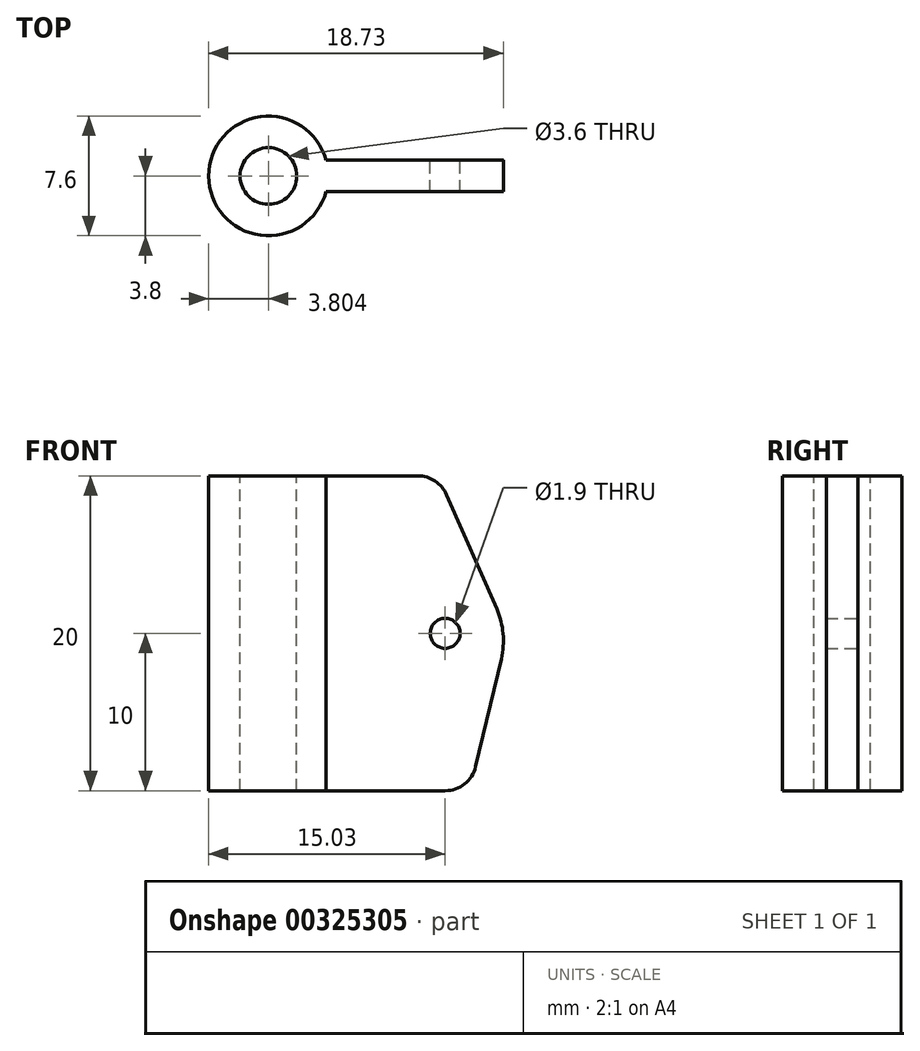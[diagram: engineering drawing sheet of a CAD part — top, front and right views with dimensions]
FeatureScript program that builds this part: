
annotation { "Feature Type Name" : "Feature", "Feature Type Description" : "" }
export const myFeature = defineFeature(function(context is Context, id is Id, definition is map)
    precondition{}
    {
        {
            var Q0;
            Q0=qCreatedBy(makeId("Front.planeOp"),FACE);
            var sketch = newSketch(context, id + "F0", { "sketchPlane" : qUnion([Q0])});
            skLineSegment(sketch, "E0.bottom", {"start": v(-13.38, 31.35) * mm, "end": v(-11.38, 31.35) * mm});
            skLineSegment(sketch, "E0.top", {"start": v(-13.38, 11.35) * mm, "end": v(-11.38, 11.35) * mm});
            skLineSegment(sketch, "E0.left", {"start": v(-13.38, 31.35) * mm, "end": v(-13.38, 11.35) * mm});
            skLineSegment(sketch, "E0.right", {"start": v(-11.38, 31.35) * mm, "end": v(-11.38, 11.35) * mm});
            skLineSegment(sketch, "E1", {"start": v(-13.38, 21.35) * mm, "end": v(0, 21.35) * mm, "construction": true});
            skPoint(sketch, "E1.endSnap0", {"position": v(-11.38, 21.35) * mm});
            skLineSegment(sketch, "E2", {"start": v(-11.38, 31.35) * mm, "end": v(-5.68, 31.35) * mm});
            skLineSegment(sketch, "E3", {"start": v(-3.85, 30.15) * mm, "end": v(-0.67, 22.88) * mm});
            skLineSegment(sketch, "E4", {"start": v(-0.39, 19.72) * mm, "end": v(-2.01, 12.89) * mm});
            skLineSegment(sketch, "E5", {"start": v(-3.96, 11.35) * mm, "end": v(-11.38, 11.35) * mm});
            skPoint(sketch, "E6.orphan", {"position": v(3.48, 21.35) * mm});
            skCircle(sketch, "E7", {"center": v(-3.95, 21.35) * mm, "radius": 0.95 * mm});
            skPoint(sketch, "E8.visualSharp", {"position": v(-4.38, 31.35) * mm});
            skArc(sketch, "E8.filletArc", {"start": v(-3.85, 30.15) * mm, "mid": v(-4.59, 31.02) * mm, "end": v(-5.68, 31.35) * mm});
            skPoint(sketch, "E9.visualSharp", {"position": v(-2.38, 11.35) * mm});
            skArc(sketch, "E9.filletArc", {"start": v(-3.96, 11.35) * mm, "mid": v(-2.72, 11.78) * mm, "end": v(-2.01, 12.89) * mm});
            skPoint(sketch, "E10.visualSharp", {"position": v(0, 21.35) * mm});
            skArc(sketch, "E10.filletArc", {"start": v(-0.39, 19.72) * mm, "mid": v(-0.27, 21.33) * mm, "end": v(-0.67, 22.88) * mm});
            skLineSegment(sketch, "E11", {"start": v(-15.18, 34.35) * mm, "end": v(-15.18, 8.54) * mm});
            skLineSegment(sketch, "E12", {"start": v(-12.08, 31.35) * mm, "end": v(-12.08, 11.35) * mm});
            skSolve(sketch);
        }
        {
            var Q0;
            Q0=makeQuery(id+"F0.imprint","IMPRINT",FACE,{"disambiguationData":[TD([[makeQuery(id+"F0.imprint","IMPRINT",EDGE,{"derivedFrom":sQuery(id+"F0.wireOp",EDGE,"E0.bottom")}),-1.0]])]});
            var Q1;
            Q1=sQuery(id+"F0.wireOp",EDGE,"E11");
            revolve(context, id + "F1", {"entities" : qUnion([Q0]), "axis" : qUnion([Q1]), "revolveType" : RevolveType.FULL});
        }
        {
            var Q0;
            {var subQ0=sQuery(id+"F0.wireOp",EDGE,"E0.right");Q0=makeQuery(id+"F0.imprint","IMPRINT",FACE,{"disambiguationData":[TD([[makeQuery(id+"F0.imprint","IMPRINT",EDGE,{"derivedFrom":subQ0}),-1.0]])]});}
            var Q1;
            Q1=makeQuery(id+"F0.imprint","IMPRINT",FACE,{"disambiguationData":[TD([[makeQuery(id+"F0.imprint","IMPRINT",EDGE,{"derivedFrom":sQuery(id+"F0.wireOp",EDGE,"E0.right")}),1.0]])]});
            extrude(context, id + "F2", {"entities" : qUnion([Q0, Q1]), "operationType" : NewBodyOperationType.ADD, "endBound" : BoundingType.SYMMETRIC, "depth" : 2 * mm});
        }
    });
